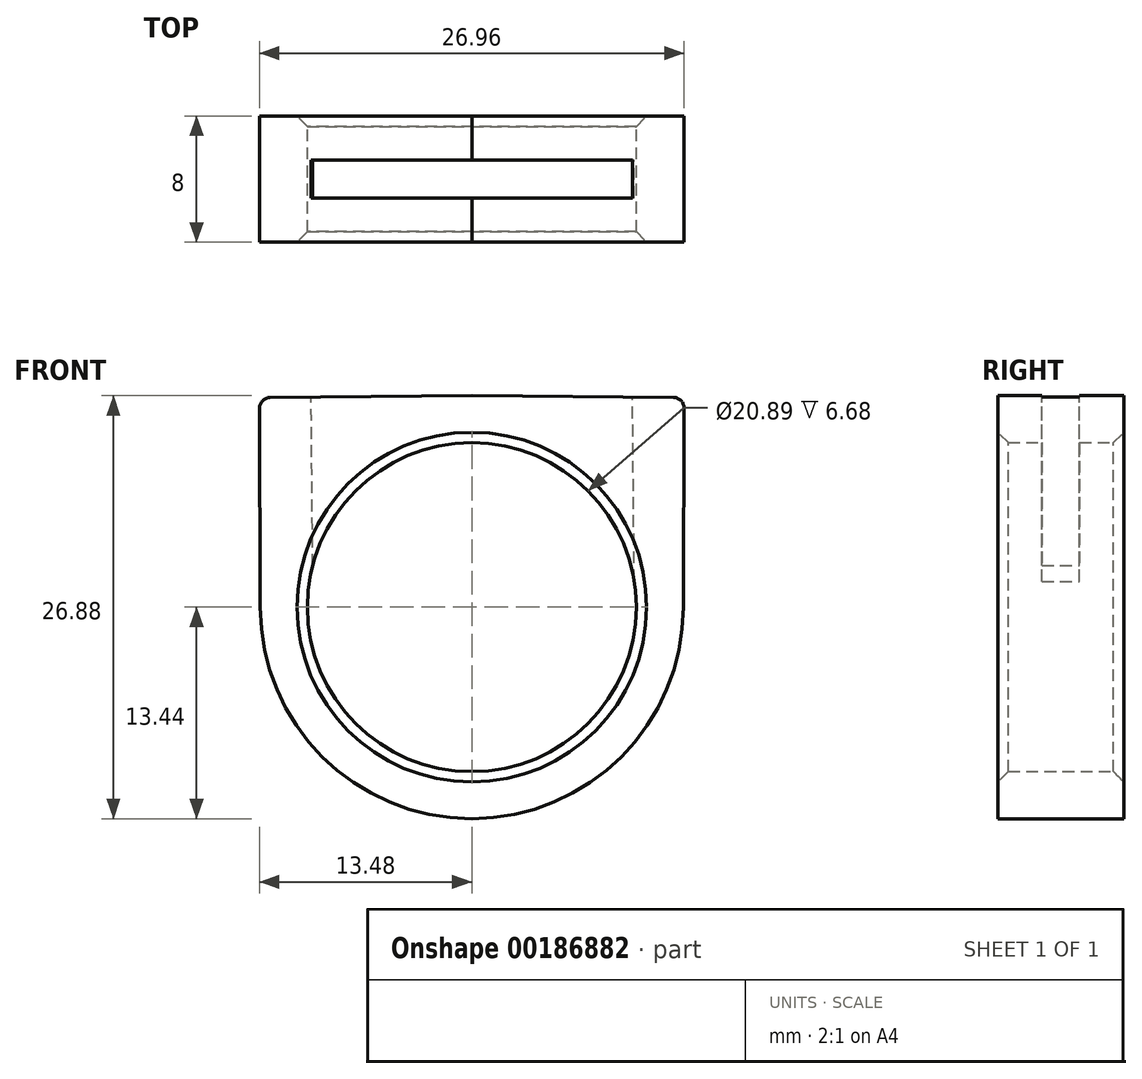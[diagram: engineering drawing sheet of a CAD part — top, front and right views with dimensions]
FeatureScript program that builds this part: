
annotation { "Feature Type Name" : "Feature", "Feature Type Description" : "" }
export const myFeature = defineFeature(function(context is Context, id is Id, definition is map)
    precondition{}
    {
        {
            var Q0;
            Q0=qCreatedBy(makeId("Front.planeOp"),FACE);
            var sketch = newSketch(context, id + "F0", { "sketchPlane" : qUnion([Q0])});
            skCircle(sketch, "E0", {"center": v(0, 0) * mm, "radius": 10.45 * mm});
            skCircle(sketch, "E1", {"center": v(0, 0) * mm, "radius": 13.44 * mm});
            skLineSegment(sketch, "E2.bottom", {"start": v(13.48, 13.31) * mm, "end": v(-13.48, 13.31) * mm});
            skLineSegment(sketch, "E2.top", {"start": v(1.83, -13.31) * mm, "end": v(-1.83, -13.31) * mm});
            skLineSegment(sketch, "E3", {"start": v(-13.48, 13.31) * mm, "end": v(0, 13.44) * mm});
            skPoint(sketch, "E3.endSnap0", {"position": v(0, 13.31) * mm});
            skLineSegment(sketch, "E4", {"start": v(0, 13.44) * mm, "end": v(13.48, 13.31) * mm});
            skLineSegment(sketch, "E5", {"start": v(13.44, 0) * mm, "end": v(-13.44, 0) * mm});
            skLineSegment(sketch, "E6", {"start": v(-13.44, 0) * mm, "end": v(-13.48, 13.31) * mm});
            skPoint(sketch, "E2.left.end.orphan", {"position": v(13.48, -13.31) * mm});
            skPoint(sketch, "E2.right.end.orphan", {"position": v(-13.48, -13.31) * mm});
            skLineSegment(sketch, "E7", {"start": v(13.48, 13.31) * mm, "end": v(13.44, 0) * mm});
            skSolve(sketch);
        }
        {
            var Q0;
            Q0 = qSketchRegion(id + "F0", true);
            extrude(context, id + "F1", {"entities" : qUnion([Q0]), "depth" : 8 * mm});
        }
        {
            var Q0;
            Q0=makeQuery(id+"F1.opExtrude","SWEPT_FACE",FACE,{"disambiguationData":[OSD([sQuery(id+"F0.wireOp",EDGE,"E3")])]});
            var sketch = newSketch(context, id + "F2", { "sketchPlane" : qUnion([Q0])});
            skLineSegment(sketch, "E8.bottom", {"start": v(-10.08, -5.2) * mm, "end": v(10.33, -5.2) * mm});
            skLineSegment(sketch, "E8.top", {"start": v(-10.08, -2.8) * mm, "end": v(10.33, -2.8) * mm});
            skLineSegment(sketch, "E8.left", {"start": v(-10.08, -5.2) * mm, "end": v(-10.08, -2.8) * mm});
            skLineSegment(sketch, "E8.right", {"start": v(10.33, -5.2) * mm, "end": v(10.33, -2.8) * mm});
            skPoint(sketch, "E8.middle", {"position": v(0.12, -4) * mm});
            skSolve(sketch);
        }
        {
            var Q0;
            Q0 = qSketchRegion(id + "F2", true);
            extrude(context, id + "F3", {"entities" : qUnion([Q0]), "operationType" : NewBodyOperationType.REMOVE, "oppositeDirection" : true, "depth" : 13.1 * mm});
        }
        {
            var Q0;
            Q0=makeQuery(id+"F1.opExtrude","SWEPT_EDGE",EDGE,{"disambiguationData":[OSD([sQuery(id+"F0.wireOp",EDGE,"E2.bottom"),sQuery(id+"F0.wireOp",EDGE,"E3"),sQuery(id+"F0.wireOp",EDGE,"E6")])]});
            var Q1;
            Q1=makeQuery(id+"F1.opExtrude","SWEPT_EDGE",EDGE,{"disambiguationData":[OSD([sQuery(id+"F0.wireOp",EDGE,"E2.bottom"),sQuery(id+"F0.wireOp",EDGE,"E4"),sQuery(id+"F0.wireOp",EDGE,"E7")])]});
            fillet(context, id + "F4", {"entities" : qUnion([Q0, Q1]), "radius" : .66 * mm, "tangentPropagation" : true, "allowEdgeOverflow" : false});
        }
        {
            var Q0;
            Q0=makeQuery(id+"F1.opExtrude","CAP_EDGE",EDGE,{"disambiguationData":[OSD([sQuery(id+"F0.wireOp",EDGE,"E0")])],"isStart":true});
            var Q1;
            Q1=makeQuery(id+"F1.opExtrude","CAP_EDGE",EDGE,{"disambiguationData":[OSD([sQuery(id+"F0.wireOp",EDGE,"E0")])],"isStart":false});
            chamfer(context, id + "F5", {"entities" : qUnion([Q0, Q1]), "width" : .66 * mm, "tangentPropagation" : true});
        }
    });
